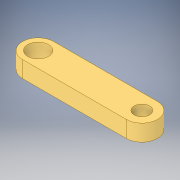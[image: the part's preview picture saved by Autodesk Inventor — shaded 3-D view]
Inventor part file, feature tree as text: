
AUTODESK INVENTOR PART (.ipt)
format: ipt  version: 2019 (Build 230136000, 136)  size: 117,760 bytes
history: native  units: mm
features: other x1, extrude x1, sketch x1
ambient origin geometry x8: Origin, YZ Plane, XZ Plane, XY Plane, X Axis, Y Axis, Z Axis, Center Point
bodies: Body1 (feature_tree)
feature tree (3):
  other  "Sólido1"
  extrude  "Extrusión1"  Depth=6.0mm
  sketch  "Boceto1"  dims[d0=20.0mm d1=6.0mm d2=4.0mm d3=3.0mm d4=3.18mm d5=0.0mm]
